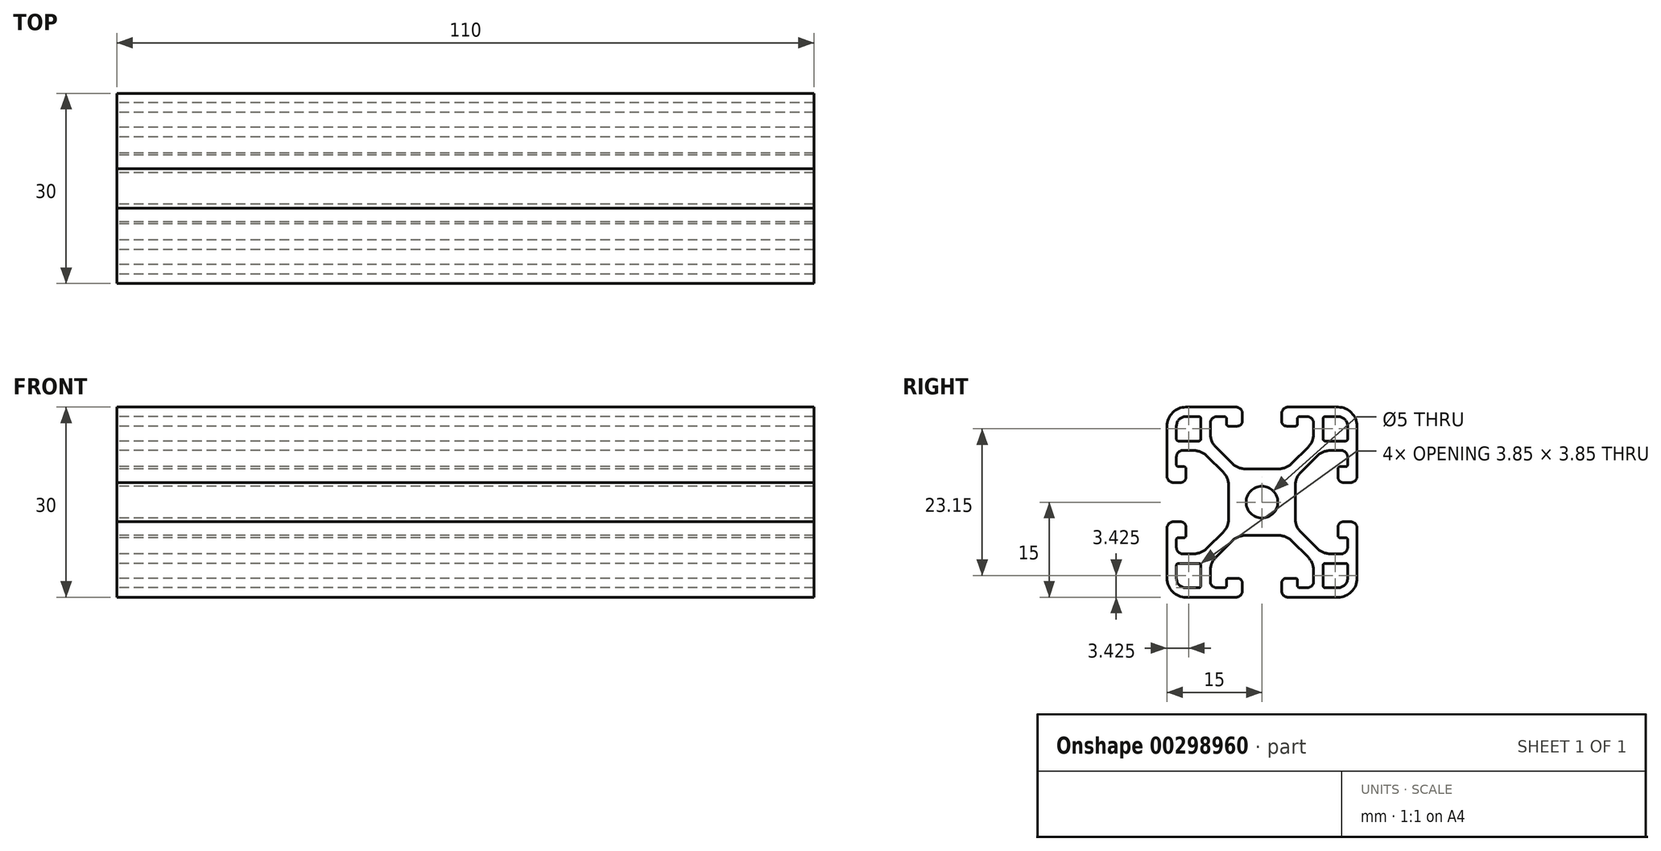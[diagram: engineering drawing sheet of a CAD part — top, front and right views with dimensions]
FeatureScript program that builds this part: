
annotation { "Feature Type Name" : "Feature", "Feature Type Description" : "" }
export const myFeature = defineFeature(function(context is Context, id is Id, definition is map)
    precondition{}
    {
        {
            var Q0;
            Q0=qCreatedBy(makeId("Right.planeOp"),FACE);
            var sketch = newSketch(context, id + "F0", { "sketchPlane" : qUnion([Q0])});
            skLineSegment(sketch, "E0", {"start": v(8.69, -7.27) * mm, "end": v(6.13, -4.71) * mm});
            skLineSegment(sketch, "E1", {"start": v(-6.13, 4.71) * mm, "end": v(-8.69, 7.27) * mm});
            skLineSegment(sketch, "E2", {"start": v(7.27, -8.69) * mm, "end": v(4.71, -6.13) * mm});
            skLineSegment(sketch, "E3", {"start": v(-4.71, 6.13) * mm, "end": v(-7.27, 8.69) * mm});
            skLineSegment(sketch, "E4", {"start": v(4.1, -15) * mm, "end": v(12, -15) * mm});
            skLineSegment(sketch, "E5", {"start": v(-12, -15) * mm, "end": v(-4.1, -15) * mm});
            skLineSegment(sketch, "E6", {"start": v(-7.15, -13.5) * mm, "end": v(-5.9, -13.5) * mm});
            skLineSegment(sketch, "E7", {"start": v(5.9, -13.5) * mm, "end": v(7.15, -13.5) * mm});
            skLineSegment(sketch, "E8", {"start": v(9.95, -13.5) * mm, "end": v(12, -13.5) * mm});
            skLineSegment(sketch, "E9", {"start": v(-12, -13.5) * mm, "end": v(-9.95, -13.5) * mm});
            skLineSegment(sketch, "E10", {"start": v(-5.3, -12) * mm, "end": v(-3.9, -12) * mm});
            skLineSegment(sketch, "E11", {"start": v(3.9, -12) * mm, "end": v(5.3, -12) * mm});
            skLineSegment(sketch, "E12", {"start": v(9.95, -9.65) * mm, "end": v(13.2, -9.65) * mm});
            skLineSegment(sketch, "E13", {"start": v(-13.2, -9.65) * mm, "end": v(-9.95, -9.65) * mm});
            skLineSegment(sketch, "E14", {"start": v(10.8, -8.15) * mm, "end": v(12.5, -8.15) * mm});
            skLineSegment(sketch, "E15", {"start": v(-12.5, -8.15) * mm, "end": v(-10.8, -8.15) * mm});
            skLineSegment(sketch, "E16", {"start": v(12.3, -5.6) * mm, "end": v(13.2, -5.6) * mm});
            skLineSegment(sketch, "E17", {"start": v(-13.2, -5.6) * mm, "end": v(-12.3, -5.6) * mm});
            skLineSegment(sketch, "E18", {"start": v(-2.6, -5.25) * mm, "end": v(2.6, -5.25) * mm});
            skLineSegment(sketch, "E19", {"start": v(12.8, -3.1) * mm, "end": v(14, -3.1) * mm});
            skLineSegment(sketch, "E20", {"start": v(-14, -3.1) * mm, "end": v(-12.8, -3.1) * mm});
            skLineSegment(sketch, "E21", {"start": v(12.8, 3.1) * mm, "end": v(14, 3.1) * mm});
            skLineSegment(sketch, "E22", {"start": v(-14, 3.1) * mm, "end": v(-12.8, 3.1) * mm});
            skLineSegment(sketch, "E23", {"start": v(-2.6, 5.25) * mm, "end": v(2.6, 5.25) * mm});
            skLineSegment(sketch, "E24", {"start": v(12.3, 5.6) * mm, "end": v(13.2, 5.6) * mm});
            skLineSegment(sketch, "E25", {"start": v(-13.2, 5.6) * mm, "end": v(-12.3, 5.6) * mm});
            skLineSegment(sketch, "E26", {"start": v(10.8, 8.15) * mm, "end": v(12.5, 8.15) * mm});
            skLineSegment(sketch, "E27", {"start": v(-12.5, 8.15) * mm, "end": v(-10.8, 8.15) * mm});
            skLineSegment(sketch, "E28", {"start": v(-13.2, 9.65) * mm, "end": v(-9.95, 9.65) * mm});
            skLineSegment(sketch, "E29", {"start": v(9.95, 9.65) * mm, "end": v(13.2, 9.65) * mm});
            skLineSegment(sketch, "E30", {"start": v(3.9, 12) * mm, "end": v(5.3, 12) * mm});
            skLineSegment(sketch, "E31", {"start": v(-5.3, 12) * mm, "end": v(-3.9, 12) * mm});
            skLineSegment(sketch, "E32", {"start": v(5.9, 13.5) * mm, "end": v(7.15, 13.5) * mm});
            skLineSegment(sketch, "E33", {"start": v(-7.15, 13.5) * mm, "end": v(-5.9, 13.5) * mm});
            skLineSegment(sketch, "E34", {"start": v(-12, 13.5) * mm, "end": v(-9.95, 13.5) * mm});
            skLineSegment(sketch, "E35", {"start": v(9.95, 13.5) * mm, "end": v(12, 13.5) * mm});
            skLineSegment(sketch, "E36", {"start": v(4.1, 15) * mm, "end": v(12, 15) * mm});
            skLineSegment(sketch, "E37", {"start": v(-12, 15) * mm, "end": v(-4.1, 15) * mm});
            skLineSegment(sketch, "E38", {"start": v(6.13, 4.71) * mm, "end": v(8.69, 7.27) * mm});
            skLineSegment(sketch, "E39", {"start": v(-7.27, -8.69) * mm, "end": v(-4.71, -6.13) * mm});
            skLineSegment(sketch, "E40", {"start": v(4.71, 6.13) * mm, "end": v(7.27, 8.69) * mm});
            skLineSegment(sketch, "E41", {"start": v(-8.69, -7.27) * mm, "end": v(-6.13, -4.71) * mm});
            skLineSegment(sketch, "E42", {"start": v(-15, 4.1) * mm, "end": v(-15, 12) * mm});
            skLineSegment(sketch, "E43", {"start": v(-15, -12) * mm, "end": v(-15, -4.1) * mm});
            skLineSegment(sketch, "E44", {"start": v(-13.5, 5.9) * mm, "end": v(-13.5, 7.15) * mm});
            skLineSegment(sketch, "E45", {"start": v(-13.5, -7.15) * mm, "end": v(-13.5, -5.9) * mm});
            skLineSegment(sketch, "E46", {"start": v(-13.5, 9.95) * mm, "end": v(-13.5, 12) * mm});
            skLineSegment(sketch, "E47", {"start": v(-13.5, -12) * mm, "end": v(-13.5, -9.95) * mm});
            skLineSegment(sketch, "E48", {"start": v(-12, 3.9) * mm, "end": v(-12, 5.3) * mm});
            skLineSegment(sketch, "E49", {"start": v(-12, -5.3) * mm, "end": v(-12, -3.9) * mm});
            skLineSegment(sketch, "E50", {"start": v(-9.65, 9.95) * mm, "end": v(-9.65, 13.2) * mm});
            skLineSegment(sketch, "E51", {"start": v(-9.65, -13.2) * mm, "end": v(-9.65, -9.95) * mm});
            skLineSegment(sketch, "E52", {"start": v(-8.15, 10.8) * mm, "end": v(-8.15, 12.5) * mm});
            skLineSegment(sketch, "E53", {"start": v(-8.15, -12.5) * mm, "end": v(-8.15, -10.8) * mm});
            skLineSegment(sketch, "E54", {"start": v(-5.6, 12.3) * mm, "end": v(-5.6, 13.2) * mm});
            skLineSegment(sketch, "E55", {"start": v(-5.6, -13.2) * mm, "end": v(-5.6, -12.3) * mm});
            skLineSegment(sketch, "E56", {"start": v(-5.25, -2.6) * mm, "end": v(-5.25, 2.6) * mm});
            skLineSegment(sketch, "E57", {"start": v(-3.1, 12.8) * mm, "end": v(-3.1, 14) * mm});
            skLineSegment(sketch, "E58", {"start": v(-3.1, -14) * mm, "end": v(-3.1, -12.8) * mm});
            skLineSegment(sketch, "E59", {"start": v(3.1, -14) * mm, "end": v(3.1, -12.8) * mm});
            skLineSegment(sketch, "E60", {"start": v(3.1, 12.8) * mm, "end": v(3.1, 14) * mm});
            skLineSegment(sketch, "E61", {"start": v(5.25, -2.6) * mm, "end": v(5.25, 2.6) * mm});
            skLineSegment(sketch, "E62", {"start": v(5.6, 12.3) * mm, "end": v(5.6, 13.2) * mm});
            skLineSegment(sketch, "E63", {"start": v(5.6, -13.2) * mm, "end": v(5.6, -12.3) * mm});
            skLineSegment(sketch, "E64", {"start": v(8.15, 10.8) * mm, "end": v(8.15, 12.5) * mm});
            skLineSegment(sketch, "E65", {"start": v(8.15, -12.5) * mm, "end": v(8.15, -10.8) * mm});
            skLineSegment(sketch, "E66", {"start": v(9.65, 9.95) * mm, "end": v(9.65, 13.2) * mm});
            skLineSegment(sketch, "E67", {"start": v(9.65, -13.2) * mm, "end": v(9.65, -9.95) * mm});
            skLineSegment(sketch, "E68", {"start": v(12, -5.3) * mm, "end": v(12, -3.9) * mm});
            skLineSegment(sketch, "E69", {"start": v(12, 3.9) * mm, "end": v(12, 5.3) * mm});
            skLineSegment(sketch, "E70", {"start": v(13.5, -7.15) * mm, "end": v(13.5, -5.9) * mm});
            skLineSegment(sketch, "E71", {"start": v(13.5, 5.9) * mm, "end": v(13.5, 7.15) * mm});
            skLineSegment(sketch, "E72", {"start": v(13.5, 9.95) * mm, "end": v(13.5, 12) * mm});
            skLineSegment(sketch, "E73", {"start": v(13.5, -12) * mm, "end": v(13.5, -9.95) * mm});
            skLineSegment(sketch, "E74", {"start": v(15, -12) * mm, "end": v(15, -4.1) * mm});
            skLineSegment(sketch, "E75", {"start": v(15, 4.1) * mm, "end": v(15, 12) * mm});
            skArc(sketch, "E76", {"start": v(-14, -3.1) * mm, "mid": v(-14.7, -3.4) * mm, "end": v(-15, -4.1) * mm});
            skArc(sketch, "E77", {"start": v(-15, 4.1) * mm, "mid": v(-14.7, 3.4) * mm, "end": v(-14, 3.1) * mm});
            skArc(sketch, "E78", {"start": v(-13.2, -9.65) * mm, "mid": v(-13.41, -9.74) * mm, "end": v(-13.5, -9.95) * mm});
            skArc(sketch, "E79", {"start": v(-13.2, -5.6) * mm, "mid": v(-13.41, -5.69) * mm, "end": v(-13.5, -5.9) * mm});
            skArc(sketch, "E80", {"start": v(-13.5, 5.9) * mm, "mid": v(-13.41, 5.69) * mm, "end": v(-13.2, 5.6) * mm});
            skArc(sketch, "E81", {"start": v(-13.5, 9.95) * mm, "mid": v(-13.41, 9.74) * mm, "end": v(-13.2, 9.65) * mm});
            skArc(sketch, "E82", {"start": v(-12, -3.9) * mm, "mid": v(-12.23, -3.33) * mm, "end": v(-12.8, -3.1) * mm});
            skArc(sketch, "E83", {"start": v(-12.8, 3.1) * mm, "mid": v(-12.23, 3.33) * mm, "end": v(-12, 3.9) * mm});
            skArc(sketch, "E84", {"start": v(-13.5, -7.15) * mm, "mid": v(-13.2, -7.86) * mm, "end": v(-12.5, -8.15) * mm});
            skArc(sketch, "E85", {"start": v(-12.5, 8.15) * mm, "mid": v(-13.2, 7.86) * mm, "end": v(-13.5, 7.15) * mm});
            skArc(sketch, "E86", {"start": v(-12.3, -5.6) * mm, "mid": v(-12.09, -5.51) * mm, "end": v(-12, -5.3) * mm});
            skArc(sketch, "E87", {"start": v(-12, 5.3) * mm, "mid": v(-12.09, 5.51) * mm, "end": v(-12.3, 5.6) * mm});
            skArc(sketch, "E88", {"start": v(-13.5, -12) * mm, "mid": v(-13.06, -13.06) * mm, "end": v(-12, -13.5) * mm});
            skArc(sketch, "E89", {"start": v(-15, -12) * mm, "mid": v(-14.12, -14.12) * mm, "end": v(-12, -15) * mm});
            skArc(sketch, "E90", {"start": v(-12, 13.5) * mm, "mid": v(-13.06, 13.06) * mm, "end": v(-13.5, 12) * mm});
            skArc(sketch, "E91", {"start": v(-12, 15) * mm, "mid": v(-14.12, 14.12) * mm, "end": v(-15, 12) * mm});
            skArc(sketch, "E92", {"start": v(-10.8, -8.15) * mm, "mid": v(-9.66, -7.92) * mm, "end": v(-8.69, -7.27) * mm});
            skArc(sketch, "E93", {"start": v(-8.69, 7.27) * mm, "mid": v(-9.66, 7.92) * mm, "end": v(-10.8, 8.15) * mm});
            skArc(sketch, "E94", {"start": v(-9.95, -13.5) * mm, "mid": v(-9.74, -13.41) * mm, "end": v(-9.65, -13.2) * mm});
            skArc(sketch, "E95", {"start": v(-9.65, -9.95) * mm, "mid": v(-9.74, -9.74) * mm, "end": v(-9.95, -9.65) * mm});
            skArc(sketch, "E96", {"start": v(-9.95, 9.65) * mm, "mid": v(-9.74, 9.74) * mm, "end": v(-9.65, 9.95) * mm});
            skArc(sketch, "E97", {"start": v(-9.65, 13.2) * mm, "mid": v(-9.74, 13.41) * mm, "end": v(-9.95, 13.5) * mm});
            skArc(sketch, "E98", {"start": v(-6.13, -4.71) * mm, "mid": v(-5.48, -3.74) * mm, "end": v(-5.25, -2.6) * mm});
            skArc(sketch, "E99", {"start": v(-5.25, 2.6) * mm, "mid": v(-5.48, 3.74) * mm, "end": v(-6.13, 4.71) * mm});
            skArc(sketch, "E100", {"start": v(-8.15, -12.5) * mm, "mid": v(-7.86, -13.2) * mm, "end": v(-7.15, -13.5) * mm});
            skArc(sketch, "E101", {"start": v(-7.15, 13.5) * mm, "mid": v(-7.86, 13.2) * mm, "end": v(-8.15, 12.5) * mm});
            skArc(sketch, "E102", {"start": v(-5.9, -13.5) * mm, "mid": v(-5.69, -13.41) * mm, "end": v(-5.6, -13.2) * mm});
            skArc(sketch, "E103", {"start": v(-5.6, 13.2) * mm, "mid": v(-5.69, 13.41) * mm, "end": v(-5.9, 13.5) * mm});
            skArc(sketch, "E104", {"start": v(-5.3, -12) * mm, "mid": v(-5.51, -12.09) * mm, "end": v(-5.6, -12.3) * mm});
            skArc(sketch, "E105", {"start": v(-5.6, 12.3) * mm, "mid": v(-5.51, 12.09) * mm, "end": v(-5.3, 12) * mm});
            skArc(sketch, "E106", {"start": v(-7.27, -8.69) * mm, "mid": v(-7.92, -9.66) * mm, "end": v(-8.15, -10.8) * mm});
            skArc(sketch, "E107", {"start": v(-8.15, 10.8) * mm, "mid": v(-7.92, 9.66) * mm, "end": v(-7.27, 8.69) * mm});
            skArc(sketch, "E108", {"start": v(-4.1, -15) * mm, "mid": v(-3.4, -14.7) * mm, "end": v(-3.1, -14) * mm});
            skArc(sketch, "E109", {"start": v(-3.1, 14) * mm, "mid": v(-3.4, 14.7) * mm, "end": v(-4.1, 15) * mm});
            skArc(sketch, "E110", {"start": v(-3.1, -12.8) * mm, "mid": v(-3.33, -12.23) * mm, "end": v(-3.9, -12) * mm});
            skArc(sketch, "E111", {"start": v(-3.9, 12) * mm, "mid": v(-3.33, 12.23) * mm, "end": v(-3.1, 12.8) * mm});
            skArc(sketch, "E112", {"start": v(-2.6, -5.25) * mm, "mid": v(-3.74, -5.48) * mm, "end": v(-4.71, -6.13) * mm});
            skArc(sketch, "E113", {"start": v(-4.71, 6.13) * mm, "mid": v(-3.74, 5.48) * mm, "end": v(-2.6, 5.25) * mm});
            skCircle(sketch, "E114", {"center": v(0, 0) * mm, "radius": 2.5 * mm});
            skArc(sketch, "E115", {"start": v(4.71, -6.13) * mm, "mid": v(3.74, -5.48) * mm, "end": v(2.6, -5.25) * mm});
            skArc(sketch, "E116", {"start": v(2.6, 5.25) * mm, "mid": v(3.74, 5.48) * mm, "end": v(4.71, 6.13) * mm});
            skArc(sketch, "E117", {"start": v(3.9, -12) * mm, "mid": v(3.33, -12.23) * mm, "end": v(3.1, -12.8) * mm});
            skArc(sketch, "E118", {"start": v(3.1, 12.8) * mm, "mid": v(3.33, 12.23) * mm, "end": v(3.9, 12) * mm});
            skArc(sketch, "E119", {"start": v(3.1, -14) * mm, "mid": v(3.4, -14.7) * mm, "end": v(4.1, -15) * mm});
            skArc(sketch, "E120", {"start": v(4.1, 15) * mm, "mid": v(3.4, 14.7) * mm, "end": v(3.1, 14) * mm});
            skArc(sketch, "E121", {"start": v(8.15, -10.8) * mm, "mid": v(7.92, -9.66) * mm, "end": v(7.27, -8.69) * mm});
            skArc(sketch, "E122", {"start": v(7.27, 8.69) * mm, "mid": v(7.92, 9.66) * mm, "end": v(8.15, 10.8) * mm});
            skArc(sketch, "E123", {"start": v(5.6, -12.3) * mm, "mid": v(5.51, -12.09) * mm, "end": v(5.3, -12) * mm});
            skArc(sketch, "E124", {"start": v(5.3, 12) * mm, "mid": v(5.51, 12.09) * mm, "end": v(5.6, 12.3) * mm});
            skArc(sketch, "E125", {"start": v(5.6, -13.2) * mm, "mid": v(5.69, -13.41) * mm, "end": v(5.9, -13.5) * mm});
            skArc(sketch, "E126", {"start": v(5.9, 13.5) * mm, "mid": v(5.69, 13.41) * mm, "end": v(5.6, 13.2) * mm});
            skArc(sketch, "E127", {"start": v(7.15, -13.5) * mm, "mid": v(7.86, -13.2) * mm, "end": v(8.15, -12.5) * mm});
            skArc(sketch, "E128", {"start": v(8.15, 12.5) * mm, "mid": v(7.86, 13.2) * mm, "end": v(7.15, 13.5) * mm});
            skArc(sketch, "E129", {"start": v(5.25, -2.6) * mm, "mid": v(5.48, -3.74) * mm, "end": v(6.13, -4.71) * mm});
            skArc(sketch, "E130", {"start": v(6.13, 4.71) * mm, "mid": v(5.48, 3.74) * mm, "end": v(5.25, 2.6) * mm});
            skArc(sketch, "E131", {"start": v(9.65, -13.2) * mm, "mid": v(9.74, -13.41) * mm, "end": v(9.95, -13.5) * mm});
            skArc(sketch, "E132", {"start": v(9.95, -9.65) * mm, "mid": v(9.74, -9.74) * mm, "end": v(9.65, -9.95) * mm});
            skArc(sketch, "E133", {"start": v(9.65, 9.95) * mm, "mid": v(9.74, 9.74) * mm, "end": v(9.95, 9.65) * mm});
            skArc(sketch, "E134", {"start": v(9.95, 13.5) * mm, "mid": v(9.74, 13.41) * mm, "end": v(9.65, 13.2) * mm});
            skArc(sketch, "E135", {"start": v(8.69, -7.27) * mm, "mid": v(9.66, -7.92) * mm, "end": v(10.8, -8.15) * mm});
            skArc(sketch, "E136", {"start": v(10.8, 8.15) * mm, "mid": v(9.66, 7.92) * mm, "end": v(8.69, 7.27) * mm});
            skArc(sketch, "E137", {"start": v(12, -13.5) * mm, "mid": v(13.06, -13.06) * mm, "end": v(13.5, -12) * mm});
            skArc(sketch, "E138", {"start": v(12, -15) * mm, "mid": v(14.12, -14.12) * mm, "end": v(15, -12) * mm});
            skArc(sketch, "E139", {"start": v(13.5, 12) * mm, "mid": v(13.06, 13.06) * mm, "end": v(12, 13.5) * mm});
            skArc(sketch, "E140", {"start": v(15, 12) * mm, "mid": v(14.12, 14.12) * mm, "end": v(12, 15) * mm});
            skArc(sketch, "E141", {"start": v(12, -5.3) * mm, "mid": v(12.09, -5.51) * mm, "end": v(12.3, -5.6) * mm});
            skArc(sketch, "E142", {"start": v(12.3, 5.6) * mm, "mid": v(12.09, 5.51) * mm, "end": v(12, 5.3) * mm});
            skArc(sketch, "E143", {"start": v(12.5, -8.15) * mm, "mid": v(13.2, -7.86) * mm, "end": v(13.5, -7.15) * mm});
            skArc(sketch, "E144", {"start": v(13.5, 7.15) * mm, "mid": v(13.2, 7.86) * mm, "end": v(12.5, 8.15) * mm});
            skArc(sketch, "E145", {"start": v(12.8, -3.1) * mm, "mid": v(12.23, -3.33) * mm, "end": v(12, -3.9) * mm});
            skArc(sketch, "E146", {"start": v(12, 3.9) * mm, "mid": v(12.23, 3.33) * mm, "end": v(12.8, 3.1) * mm});
            skArc(sketch, "E147", {"start": v(13.5, -9.95) * mm, "mid": v(13.41, -9.74) * mm, "end": v(13.2, -9.65) * mm});
            skArc(sketch, "E148", {"start": v(13.5, -5.9) * mm, "mid": v(13.41, -5.69) * mm, "end": v(13.2, -5.6) * mm});
            skArc(sketch, "E149", {"start": v(13.2, 5.6) * mm, "mid": v(13.41, 5.69) * mm, "end": v(13.5, 5.9) * mm});
            skArc(sketch, "E150", {"start": v(13.2, 9.65) * mm, "mid": v(13.41, 9.74) * mm, "end": v(13.5, 9.95) * mm});
            skArc(sketch, "E151", {"start": v(15, -4.1) * mm, "mid": v(14.7, -3.4) * mm, "end": v(14, -3.1) * mm});
            skArc(sketch, "E152", {"start": v(14, 3.1) * mm, "mid": v(14.7, 3.4) * mm, "end": v(15, 4.1) * mm});
            skLineSegment(sketch, "E153", {"start": v(0, 15) * mm, "end": v(0, -15) * mm});
            skLineSegment(sketch, "E154", {"start": v(-15, 0) * mm, "end": v(15, 0) * mm});
            skSolve(sketch);
        }
        {
            var Q0;
            Q0 = qSketchRegion(id + "F0", true);
            extrude(context, id + "F1", {"entities" : qUnion([Q0]), "endBound" : BoundingType.SYMMETRIC, "depth" : 110 * mm, "hasSecondDirection" : true, "secondDirectionOppositeDirection" : true, "secondDirectionDepth" : 40 * mm});
        }
    });
